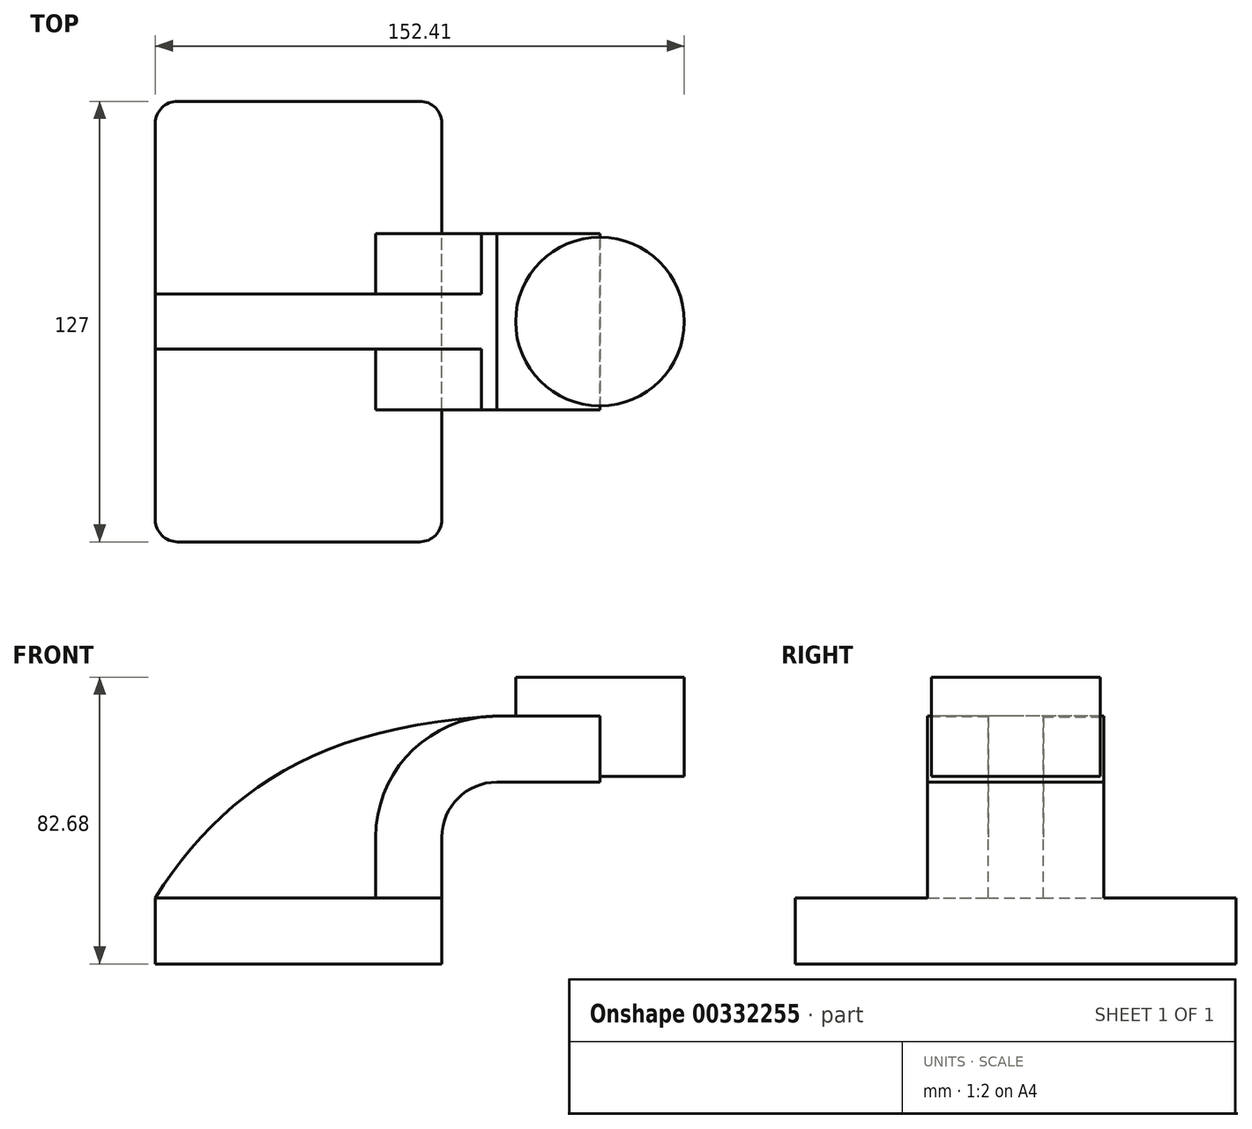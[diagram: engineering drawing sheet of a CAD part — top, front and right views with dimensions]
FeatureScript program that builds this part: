
annotation { "Feature Type Name" : "Feature", "Feature Type Description" : "" }
export const myFeature = defineFeature(function(context is Context, id is Id, definition is map)
    precondition{}
    {
        {
            var Q0;
            Q0=qCreatedBy(makeId("Front.planeOp"),FACE);
            var sketch = newSketch(context, id + "F0", { "sketchPlane" : qUnion([Q0])});
            skLineSegment(sketch, "E0.bottom", {"start": v(41.28, -9.52) * mm, "end": v(-41.28, -9.53) * mm});
            skLineSegment(sketch, "E0.top", {"start": v(41.27, 9.53) * mm, "end": v(-41.28, 9.53) * mm});
            skLineSegment(sketch, "E0.left", {"start": v(41.28, -9.52) * mm, "end": v(41.28, 9.53) * mm});
            skLineSegment(sketch, "E0.right", {"start": v(-41.28, -9.53) * mm, "end": v(-41.28, 9.53) * mm});
            skPoint(sketch, "E0.middle", {"position": v(0, 0) * mm});
            skLineSegment(sketch, "E1.bottom", {"start": v(60.33, 44.57) * mm, "end": v(111.12, 44.57) * mm});
            skLineSegment(sketch, "E1.top", {"start": v(60.32, 73.15) * mm, "end": v(111.12, 73.15) * mm});
            skLineSegment(sketch, "E1.left", {"start": v(60.33, 44.57) * mm, "end": v(60.32, 73.15) * mm});
            skLineSegment(sketch, "E1.right", {"start": v(111.12, 44.57) * mm, "end": v(111.12, 73.15) * mm});
            skPoint(sketch, "E1.middle", {"position": v(85.72, 58.86) * mm});
            skLineSegment(sketch, "E2", {"start": v(41.27, 9.53) * mm, "end": v(41.27, 27) * mm});
            skArc(sketch, "E3", {"start": v(41.27, 27) * mm, "mid": v(45.92, 38.23) * mm, "end": v(57.15, 42.88) * mm});
            skLineSegment(sketch, "E4", {"start": v(57.15, 42.88) * mm, "end": v(86.83, 42.88) * mm});
            skLineSegment(sketch, "E5.0", {"start": v(57.15, 61.93) * mm, "end": v(86.83, 61.93) * mm});
            skArc(sketch, "E5.1", {"start": v(22.23, 27) * mm, "mid": v(32.45, 51.7) * mm, "end": v(57.15, 61.93) * mm});
            skLineSegment(sketch, "E5.2", {"start": v(22.22, 9.53) * mm, "end": v(22.22, 27) * mm});
            skLineSegment(sketch, "E6", {"start": v(86.83, 42.88) * mm, "end": v(86.83, 73.15) * mm});
            skPoint(sketch, "E6.endSnap0", {"position": v(85.72, 73.15) * mm});
            skFitSpline(sketch, "E7", {"points": [v(-41.28, 9.53) * mm, v(57.15, 61.93) * mm], "startDerivative": vector(56.7, 89.22) * mm, "endDerivative": vector(159.6, 8.75) * mm});
            skSolve(sketch);
        }
        {
            var Q0;
            Q0=makeQuery(id+"F0.imprint","IMPRINT",FACE,{"disambiguationData":[TD([[makeQuery(id+"F0.imprint","IMPRINT",EDGE,{"derivedFrom":sQuery(id+"F0.wireOp",EDGE,"E0.bottom")}),-1.0]])]});
            extrude(context, id + "F1", {"entities" : qUnion([Q0]), "endBound" : BoundingType.SYMMETRIC, "depth" : 127 * mm});
        }
        {
            var Q0;
            {var subQ13=sQuery(id+"F0.wireOp",EDGE,"E2");Q0=makeQuery(id+"F0.imprint","IMPRINT",FACE,{"disambiguationData":[TD([[makeQuery(id+"F0.imprint","IMPRINT",EDGE,{"derivedFrom":subQ13}),1.0]])]});}
            var Q1;
            {var subQ0=sQuery(id+"F0.wireOp",EDGE,"E1.left");var subQ1=sQuery(id+"F0.wireOp",EDGE,"E1.bottom");var subQ2=makeQuery(id+"F0.imprint","INTERSECT",VERTEX,{"derivedFrom":[subQ1,subQ0]});Q1=makeQuery(id+"F0.imprint","IMPRINT",FACE,{"disambiguationData":[TD([[makeQuery(id+"F0.imprint","IMPRINT",EDGE,{"disambiguationData":[TD([[subQ2,-1.0]])],"derivedFrom":subQ1}),1.0]])]});}
            extrude(context, id + "F2", {"entities" : qUnion([Q0, Q1]), "operationType" : NewBodyOperationType.ADD, "endBound" : BoundingType.SYMMETRIC, "depth" : 50.8 * mm});
        }
        {
            var Q0;
            {var subQ3=sQuery(id+"F0.wireOp",EDGE,"E5.2");Q0=makeQuery(id+"F0.imprint","IMPRINT",FACE,{"disambiguationData":[TD([[makeQuery(id+"F0.imprint","IMPRINT",EDGE,{"derivedFrom":subQ3}),1.0]])]});}
            extrude(context, id + "F3", {"entities" : qUnion([Q0]), "operationType" : NewBodyOperationType.ADD, "endBound" : BoundingType.SYMMETRIC, "depth" : 15.88 * mm});
        }
        {
            var Q0;
            {var subQ0=sQuery(id+"F0.wireOp",EDGE,"E1.right");Q0=makeQuery(id+"F0.imprint","IMPRINT",FACE,{"disambiguationData":[TD([[makeQuery(id+"F0.imprint","IMPRINT",EDGE,{"derivedFrom":subQ0}),1.0]])]});}
            var Q1;
            Q1=sQuery(id+"F0.wireOp",EDGE,"E6");
            revolve(context, id + "F4", {"operationType" : NewBodyOperationType.ADD, "entities" : qUnion([Q0]), "axis" : qUnion([Q1]), "revolveType" : RevolveType.FULL});
        }
        {
            var Q0;
            Q0=makeQuery(id+"F1.opExtrude","CAP_EDGE",EDGE,{"disambiguationData":[OSD([sQuery(id+"F0.wireOp",EDGE,"E0.left")])],"isStart":false});
            var Q1;
            Q1=makeQuery(id+"F1.opExtrude","CAP_EDGE",EDGE,{"disambiguationData":[OSD([sQuery(id+"F0.wireOp",EDGE,"E0.right")])],"isStart":false});
            var Q2;
            Q2=makeQuery(id+"F1.opExtrude","CAP_EDGE",EDGE,{"disambiguationData":[OSD([sQuery(id+"F0.wireOp",EDGE,"E0.left")])],"isStart":true});
            var Q3;
            Q3=makeQuery(id+"F1.opExtrude","CAP_EDGE",EDGE,{"disambiguationData":[OSD([sQuery(id+"F0.wireOp",EDGE,"E0.right")])],"isStart":true});
            fillet(context, id + "F5", {"entities" : qUnion([Q0, Q1, Q2, Q3]), "radius" : 6.35 * mm, "tangentPropagation" : true, "allowEdgeOverflow" : false});
        }
    });
